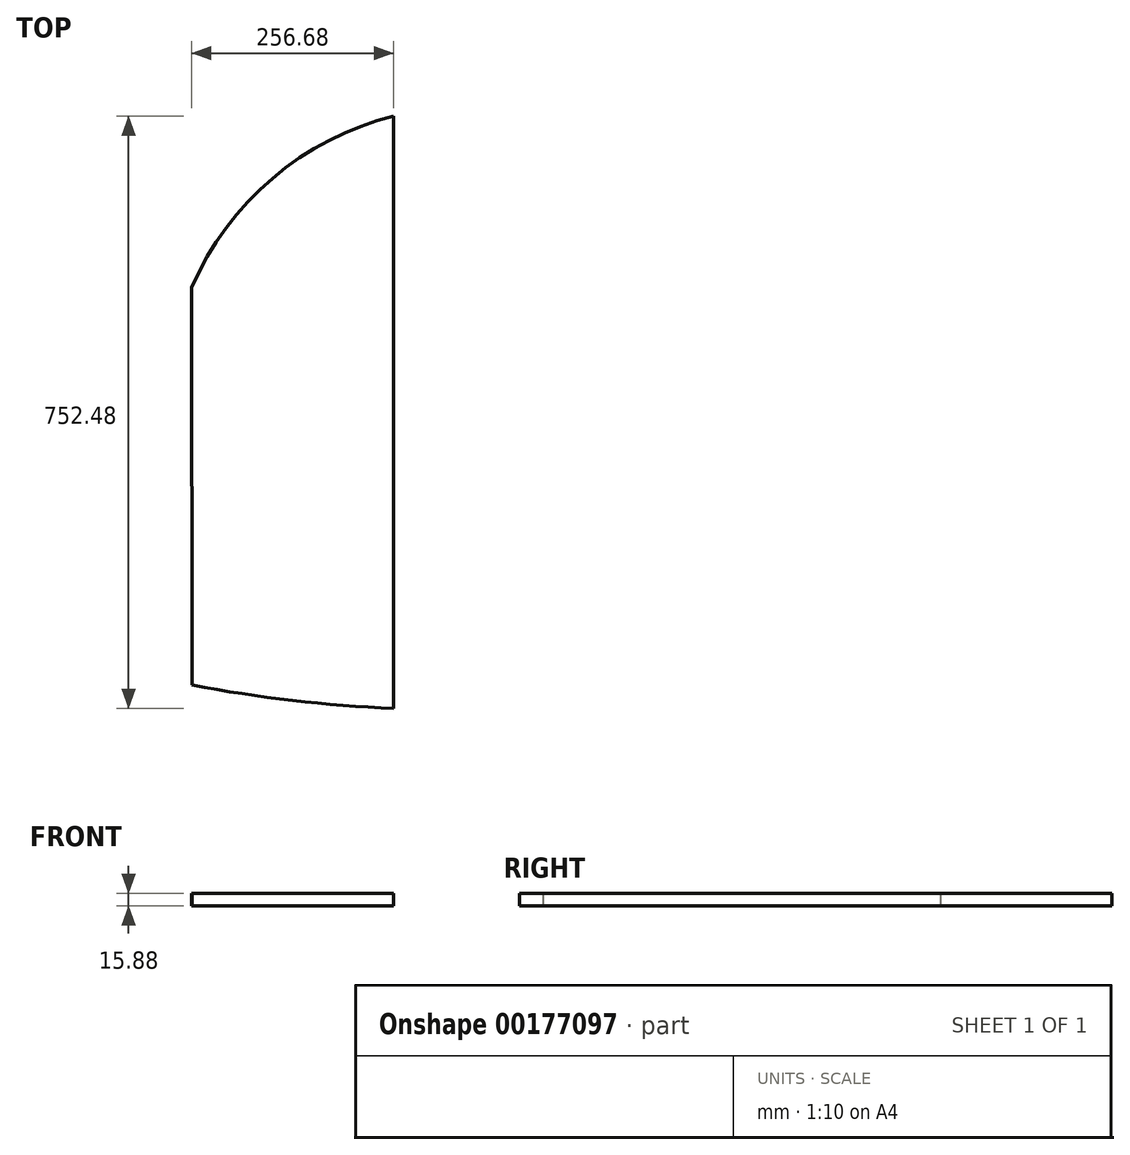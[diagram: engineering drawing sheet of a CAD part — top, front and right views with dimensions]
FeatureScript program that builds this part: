
annotation { "Feature Type Name" : "Feature", "Feature Type Description" : "" }
export const myFeature = defineFeature(function(context is Context, id is Id, definition is map)
    precondition{}
    {
        {
            var Q0;
            Q0=qCreatedBy(makeId("Top.planeOp"),FACE);
            var sketch = newSketch(context, id + "F0", { "sketchPlane" : qUnion([Q0])});
            skLineSegment(sketch, "E0", {"start": v(0, 0) * mm, "end": v(0, 752.48) * mm});
            skArc(sketch, "E1", {"start": v(-256, 29.49) * mm, "mid": v(-128.53, 10.1) * mm, "end": v(0, 0) * mm});
            skArc(sketch, "E2", {"start": v(0, 752.48) * mm, "mid": v(-153.75, 673.32) * mm, "end": v(-256.68, 534.35) * mm});
            skLineSegment(sketch, "E3", {"start": v(-256, 29.49) * mm, "end": v(-256.68, 534.35) * mm});
            skSolve(sketch);
        }
        {
            var Q0;
            Q0 = qSketchRegion(id + "F0", true);
            extrude(context, id + "F1", {"entities" : qUnion([Q0]), "depth" : 15.88 * mm});
        }
    });
